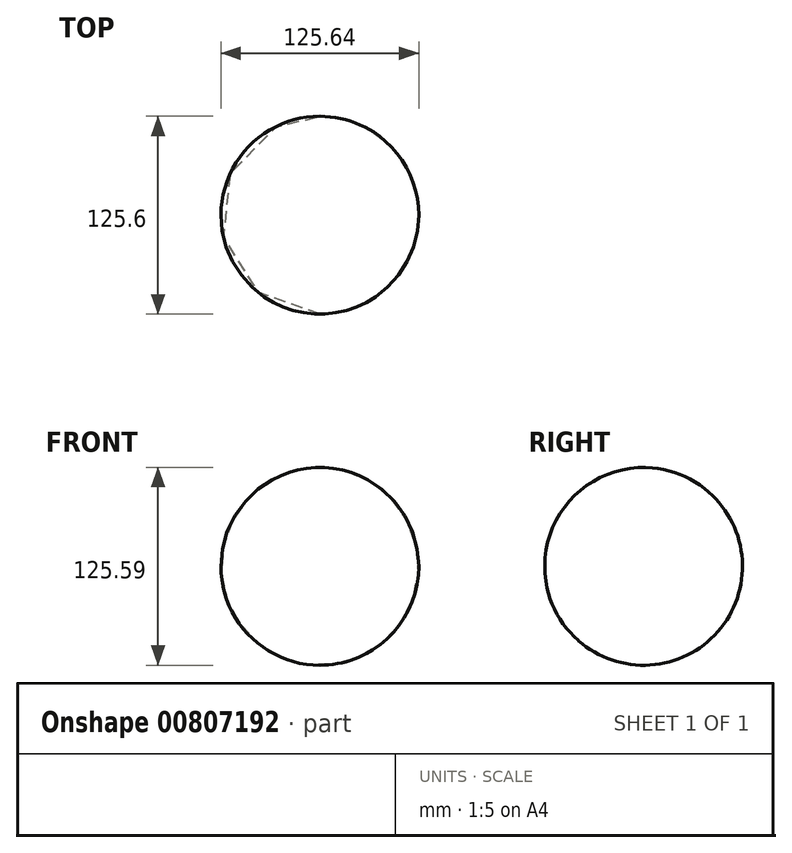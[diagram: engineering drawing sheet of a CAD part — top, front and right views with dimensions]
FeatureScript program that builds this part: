
annotation { "Feature Type Name" : "Feature", "Feature Type Description" : "" }
export const myFeature = defineFeature(function(context is Context, id is Id, definition is map)
    precondition{}
    {
        {
            var Q0;
            Q0=qCreatedBy(makeId("Right.planeOp"),FACE);
            var sketch = newSketch(context, id + "F0", { "sketchPlane" : qUnion([Q0])});
            skCircle(sketch, "E0", {"center": v(0, 0) * mm, "radius": 62.74 * mm});
            skLineSegment(sketch, "E1", {"start": v(50.06, 57.16) * mm, "end": v(-53.2, -60.48) * mm});
            skSolve(sketch);
        }
        {
            var Q0;
            {var subQ0=sQuery(id+"F0.wireOp",EDGE,"E1");var subQ1=sQuery(id+"F0.wireOp",EDGE,"E0");var subQ2=makeQuery(id+"F0.imprint","INTERSECT",VERTEX,{"disambiguationData":[OD(0.0)],"derivedFrom":[subQ1,subQ0]});Q0=makeQuery(id+"F0.imprint","IMPRINT",FACE,{"disambiguationData":[TD([[makeQuery(id+"F0.imprint","IMPRINT",EDGE,{"disambiguationData":[TD([[subQ2,-1.0]])],"derivedFrom":subQ1}),1.0]])]});}
            var Q1;
            Q1=sQuery(id+"F0.wireOp",EDGE,"E1");
            revolve(context, id + "F1", {"surfaceOperationType" : NewSurfaceOperationType.NEW, "entities" : qUnion([Q0]), "axis" : qUnion([Q1]), "revolveType" : RevolveType.SYMMETRIC, "oppositeDirection" : true, "angle" : 360 * degree});
        }
    });
